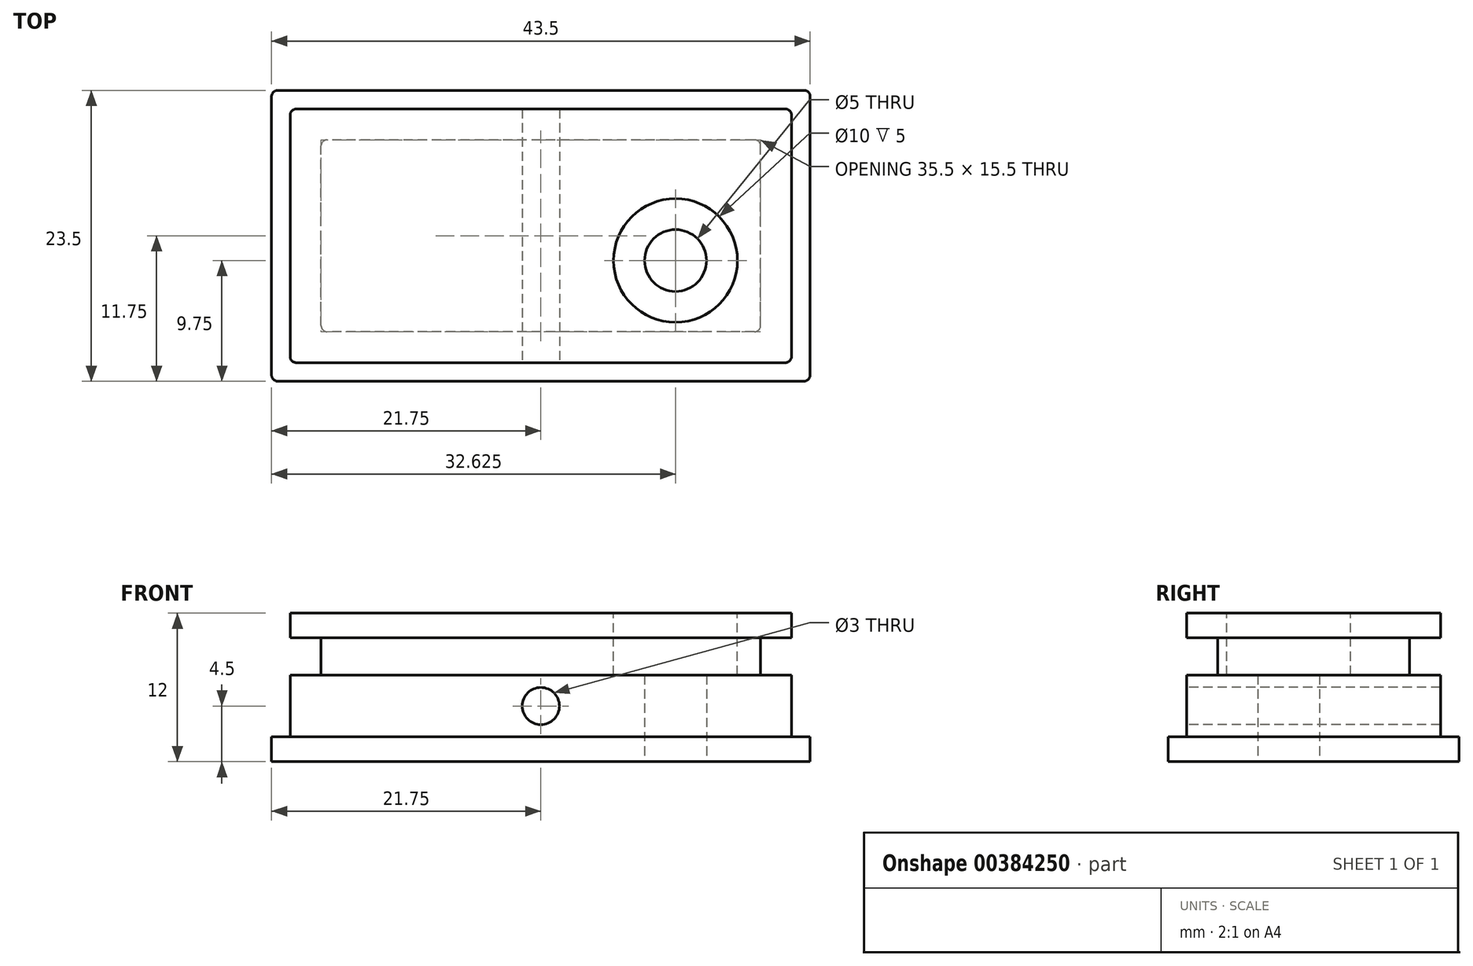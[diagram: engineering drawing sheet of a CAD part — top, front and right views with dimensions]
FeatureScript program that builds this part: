
annotation { "Feature Type Name" : "Feature", "Feature Type Description" : "" }
export const myFeature = defineFeature(function(context is Context, id is Id, definition is map)
    precondition{}
    {
        {
            var Q0;
            Q0=qCreatedBy(makeId("Top.planeOp"),FACE);
            var sketch = newSketch(context, id + "F0", { "sketchPlane" : qUnion([Q0])});
            skLineSegment(sketch, "E0.bottom", {"start": v(21.75, -11.75) * mm, "end": v(-21.75, -11.75) * mm});
            skLineSegment(sketch, "E0.top", {"start": v(21.75, 11.75) * mm, "end": v(-21.75, 11.75) * mm});
            skLineSegment(sketch, "E0.left", {"start": v(21.75, -11.75) * mm, "end": v(21.75, 11.75) * mm});
            skLineSegment(sketch, "E0.right", {"start": v(-21.75, -11.75) * mm, "end": v(-21.75, 11.75) * mm});
            skPoint(sketch, "E0.middle", {"position": v(0, 0) * mm});
            skSolve(sketch);
        }
        {
            var Q0;
            Q0=qSketchRegion(id+"F0",true);
            extrude(context, id + "F1", {"entities" : qUnion([Q0]), "depth" : 2 * mm});
        }
        {
            var Q0;
            Q0=makeQuery(id+"F1.opExtrude","CAP_FACE",FACE,{"disambiguationData":[OSD([sQuery(id+"F0.wireOp",EDGE,"E0.bottom"),sQuery(id+"F0.wireOp",EDGE,"E0.top"),sQuery(id+"F0.wireOp",EDGE,"E0.left"),sQuery(id+"F0.wireOp",EDGE,"E0.right")])],"isStart":false});
            var sketch = newSketch(context, id + "F2", { "sketchPlane" : qUnion([Q0])});
            skLineSegment(sketch, "E1.bottom", {"start": v(21.75, -11.75) * mm, "end": v(-21.75, -11.75) * mm, "construction": true});
            skLineSegment(sketch, "E1.top", {"start": v(21.75, 11.75) * mm, "end": v(-21.75, 11.75) * mm, "construction": true});
            skLineSegment(sketch, "E1.left", {"start": v(21.75, -11.75) * mm, "end": v(21.75, 11.75) * mm, "construction": true});
            skLineSegment(sketch, "E1.right", {"start": v(-21.75, -11.75) * mm, "end": v(-21.75, 11.75) * mm, "construction": true});
            skPoint(sketch, "E1.middle", {"position": v(0, 0) * mm});
            skLineSegment(sketch, "E2.0", {"start": v(20.25, 10.25) * mm, "end": v(-20.25, 10.25) * mm});
            skLineSegment(sketch, "E2.1", {"start": v(20.25, -10.25) * mm, "end": v(20.25, 10.25) * mm});
            skLineSegment(sketch, "E2.2", {"start": v(20.25, -10.25) * mm, "end": v(-20.25, -10.25) * mm});
            skLineSegment(sketch, "E2.3", {"start": v(-20.25, -10.25) * mm, "end": v(-20.25, 10.25) * mm});
            skSolve(sketch);
        }
        {
            var Q0;
            Q0=qSketchRegion(id+"F2",true);
            extrude(context, id + "F3", {"entities" : qUnion([Q0]), "operationType" : NewBodyOperationType.ADD, "depth" : 5 * mm});
        }
        {
            var Q0;
            Q0=makeQuery(id+"F3.opExtrude","CAP_FACE",FACE,{"disambiguationData":[OSD([sQuery(id+"F2.wireOp",EDGE,"E2.0"),sQuery(id+"F2.wireOp",EDGE,"E2.1"),sQuery(id+"F2.wireOp",EDGE,"E2.2"),sQuery(id+"F2.wireOp",EDGE,"E2.3")])],"isStart":false});
            var sketch = newSketch(context, id + "F4", { "sketchPlane" : qUnion([Q0])});
            skLineSegment(sketch, "E3.0", {"start": v(20.25, -10.25) * mm, "end": v(-20.25, -10.25) * mm, "construction": true});
            skLineSegment(sketch, "E4.0", {"start": v(-20.25, -10.25) * mm, "end": v(-20.25, 10.25) * mm, "construction": true});
            skLineSegment(sketch, "E5.0", {"start": v(20.25, 10.25) * mm, "end": v(-20.25, 10.25) * mm, "construction": true});
            skLineSegment(sketch, "E6.0", {"start": v(20.25, -10.25) * mm, "end": v(20.25, 10.25) * mm, "construction": true});
            skLineSegment(sketch, "E7.0", {"start": v(-17.75, -7.75) * mm, "end": v(-17.75, 7.75) * mm});
            skLineSegment(sketch, "E7.1", {"start": v(17.75, -7.75) * mm, "end": v(-17.75, -7.75) * mm});
            skLineSegment(sketch, "E7.2", {"start": v(17.75, -7.75) * mm, "end": v(17.75, 7.75) * mm});
            skLineSegment(sketch, "E7.3", {"start": v(17.75, 7.75) * mm, "end": v(-17.75, 7.75) * mm});
            skSolve(sketch);
        }
        {
            var Q0;
            Q0=qSketchRegion(id+"F4",true);
            var Q1;
            Q1=qConstructionFilter(qBodyType(qCreatedBy(id+"F4",EDGE),BodyType.WIRE),ConstructionObject.NO);
            extrude(context, id + "F5", {"entities" : qUnion([Q0]), "operationType" : NewBodyOperationType.ADD, "surfaceEntities" : qUnion([Q1]), "depth" : 3 * mm});
        }
        {
            var Q0;
            Q0=makeQuery(id+"F5.opExtrude","CAP_FACE",FACE,{"disambiguationData":[OSD([sQuery(id+"F4.wireOp",EDGE,"E7.0"),sQuery(id+"F4.wireOp",EDGE,"E7.1"),sQuery(id+"F4.wireOp",EDGE,"E7.2"),sQuery(id+"F4.wireOp",EDGE,"E7.3")])],"isStart":false});
            var sketch = newSketch(context, id + "F6", { "sketchPlane" : qUnion([Q0])});
            skLineSegment(sketch, "E8.0", {"start": v(20.25, -10.25) * mm, "end": v(-20.25, -10.25) * mm});
            skLineSegment(sketch, "E9.0", {"start": v(20.25, -10.25) * mm, "end": v(20.25, 10.25) * mm});
            skLineSegment(sketch, "E10.0", {"start": v(20.25, 10.25) * mm, "end": v(-20.25, 10.25) * mm});
            skLineSegment(sketch, "E10.1", {"start": v(-20.25, -10.25) * mm, "end": v(-20.25, 10.25) * mm});
            skSolve(sketch);
        }
        {
            var Q0;
            Q0=qSketchRegion(id+"F6",true);
            extrude(context, id + "F7", {"entities" : qUnion([Q0]), "operationType" : NewBodyOperationType.ADD, "depth" : 2 * mm});
        }
        {
            var Q0;
            Q0=makeQuery(id+"F3.opExtrude","SWEPT_EDGE",EDGE,{"disambiguationData":[OSD([sQuery(id+"F2.wireOp",EDGE,"E2.0"),sQuery(id+"F2.wireOp",EDGE,"E2.3")])]});
            var Q1;
            Q1=makeQuery(id+"F5.opExtrude","SWEPT_EDGE",EDGE,{"disambiguationData":[OSD([sQuery(id+"F4.wireOp",EDGE,"E7.0"),sQuery(id+"F4.wireOp",EDGE,"E7.3")])]});
            var Q2;
            Q2=makeQuery(id+"F7.opExtrude","SWEPT_EDGE",EDGE,{"disambiguationData":[OSD([sQuery(id+"F6.wireOp",EDGE,"E10.0"),sQuery(id+"F6.wireOp",EDGE,"E10.1")])]});
            var Q3;
            Q3=makeQuery(id+"F3.opExtrude","SWEPT_EDGE",EDGE,{"disambiguationData":[OSD([sQuery(id+"F2.wireOp",EDGE,"E2.2"),sQuery(id+"F2.wireOp",EDGE,"E2.3")])]});
            var Q4;
            Q4=makeQuery(id+"F5.opExtrude","SWEPT_EDGE",EDGE,{"disambiguationData":[OSD([sQuery(id+"F4.wireOp",EDGE,"E7.0"),sQuery(id+"F4.wireOp",EDGE,"E7.1")])]});
            var Q5;
            Q5=makeQuery(id+"F7.opExtrude","SWEPT_EDGE",EDGE,{"disambiguationData":[OSD([sQuery(id+"F6.wireOp",EDGE,"E8.0"),sQuery(id+"F6.wireOp",EDGE,"E10.1")])]});
            var Q6;
            Q6=makeQuery(id+"F3.opExtrude","SWEPT_EDGE",EDGE,{"disambiguationData":[OSD([sQuery(id+"F2.wireOp",EDGE,"E2.1"),sQuery(id+"F2.wireOp",EDGE,"E2.2")])]});
            var Q7;
            Q7=makeQuery(id+"F5.opExtrude","SWEPT_EDGE",EDGE,{"disambiguationData":[OSD([sQuery(id+"F4.wireOp",EDGE,"E7.1"),sQuery(id+"F4.wireOp",EDGE,"E7.2")])]});
            var Q8;
            Q8=makeQuery(id+"F7.opExtrude","SWEPT_EDGE",EDGE,{"disambiguationData":[OSD([sQuery(id+"F6.wireOp",EDGE,"E8.0"),sQuery(id+"F6.wireOp",EDGE,"E9.0")])]});
            var Q9;
            Q9=makeQuery(id+"F3.opExtrude","SWEPT_EDGE",EDGE,{"disambiguationData":[OSD([sQuery(id+"F2.wireOp",EDGE,"E2.0"),sQuery(id+"F2.wireOp",EDGE,"E2.1")])]});
            var Q10;
            Q10=makeQuery(id+"F5.opExtrude","SWEPT_EDGE",EDGE,{"disambiguationData":[OSD([sQuery(id+"F4.wireOp",EDGE,"E7.2"),sQuery(id+"F4.wireOp",EDGE,"E7.3")])]});
            var Q11;
            Q11=makeQuery(id+"F7.opExtrude","SWEPT_EDGE",EDGE,{"disambiguationData":[OSD([sQuery(id+"F6.wireOp",EDGE,"E9.0"),sQuery(id+"F6.wireOp",EDGE,"E10.0")])]});
            var Q12;
            Q12=makeQuery(id+"F1.opExtrude","SWEPT_EDGE",EDGE,{"disambiguationData":[OSD([sQuery(id+"F0.wireOp",EDGE,"E0.bottom"),sQuery(id+"F0.wireOp",EDGE,"E0.left")])]});
            var Q13;
            Q13=makeQuery(id+"F1.opExtrude","SWEPT_EDGE",EDGE,{"disambiguationData":[OSD([sQuery(id+"F0.wireOp",EDGE,"E0.top"),sQuery(id+"F0.wireOp",EDGE,"E0.left")])]});
            var Q14;
            Q14=makeQuery(id+"F1.opExtrude","SWEPT_EDGE",EDGE,{"disambiguationData":[OSD([sQuery(id+"F0.wireOp",EDGE,"E0.bottom"),sQuery(id+"F0.wireOp",EDGE,"E0.right")])]});
            var Q15;
            Q15=makeQuery(id+"F1.opExtrude","SWEPT_EDGE",EDGE,{"disambiguationData":[OSD([sQuery(id+"F0.wireOp",EDGE,"E0.top"),sQuery(id+"F0.wireOp",EDGE,"E0.right")])]});
            fillet(context, id + "F8", {"entities" : qUnion([Q0, Q1, Q2, Q3, Q4, Q5, Q6, Q7, Q8, Q9, Q10, Q11, Q12, Q13, Q14, Q15]), "radius" : 0.5 * mm, "tangentPropagation" : true, "allowEdgeOverflow" : false});
        }
        {
            var Q0;
            Q0=qCreatedBy(makeId("Top.planeOp"),FACE);
            var sketch = newSketch(context, id + "F9", { "sketchPlane" : qUnion([Q0])});
            skCircle(sketch, "E11", {"center": v(10.88, -2) * mm, "radius": 2.5 * mm});
            skLineSegment(sketch, "E12", {"start": v(0, -11.75) * mm, "end": v(0, 0) * mm, "construction": true});
            skLineSegment(sketch, "E13", {"start": v(0, 0) * mm, "end": v(21.75, 0) * mm, "construction": true});
            skLineSegment(sketch, "E14", {"start": v(0, -2) * mm, "end": v(21.75, -2) * mm, "construction": true});
            skLineSegment(sketch, "E15", {"start": v(10.88, 0) * mm, "end": v(10.88, -11.75) * mm, "construction": true});
            skSolve(sketch);
        }
        {
            var Q0;
            Q0=qSketchRegion(id+"F9",true);
            var Q1;
            Q1=makeQuery(id+"F7.opExtrude","CAP_FACE",FACE,{"disambiguationData":[OSD([sQuery(id+"F6.wireOp",EDGE,"E8.0"),sQuery(id+"F6.wireOp",EDGE,"E9.0"),sQuery(id+"F6.wireOp",EDGE,"E10.0"),sQuery(id+"F6.wireOp",EDGE,"E10.1")])],"isStart":false});
            extrude(context, id + "F10", {"entities" : qUnion([Q0]), "operationType" : NewBodyOperationType.REMOVE, "endBound" : BoundingType.THROUGH_ALL, "endBoundEntityFace" : qUnion([Q1]), "depth" : 25 * mm});
        }
        {
            var Q0;
            Q0=makeQuery(id+"F7.opExtrude","CAP_FACE",FACE,{"disambiguationData":[OSD([sQuery(id+"F6.wireOp",EDGE,"E8.0"),sQuery(id+"F6.wireOp",EDGE,"E9.0"),sQuery(id+"F6.wireOp",EDGE,"E10.0"),sQuery(id+"F6.wireOp",EDGE,"E10.1")])],"isStart":false});
            var sketch = newSketch(context, id + "F11", { "sketchPlane" : qUnion([Q0])});
            skCircle(sketch, "E16", {"center": v(10.88, -2) * mm, "radius": 5 * mm});
            skSolve(sketch);
        }
        {
            var Q0;
            Q0=qSketchRegion(id+"F11",true);
            var Q1;
            Q1=makeQuery(id+"F3.opExtrude","CAP_FACE",FACE,{"disambiguationData":[OSD([sQuery(id+"F2.wireOp",EDGE,"E2.0"),sQuery(id+"F2.wireOp",EDGE,"E2.1"),sQuery(id+"F2.wireOp",EDGE,"E2.2"),sQuery(id+"F2.wireOp",EDGE,"E2.3")])],"isStart":false});
            extrude(context, id + "F12", {"entities" : qUnion([Q0]), "operationType" : NewBodyOperationType.REMOVE, "endBound" : BoundingType.UP_TO_SURFACE, "oppositeDirection" : true, "endBoundEntityFace" : qUnion([Q1]), "depth" : 5.8 * mm});
        }
        {
            var Q0;
            Q0=makeQuery(id+"F3.opExtrude","SWEPT_FACE",FACE,{"disambiguationData":[OSD([sQuery(id+"F2.wireOp",EDGE,"E2.2")])]});
            var sketch = newSketch(context, id + "F13", { "sketchPlane" : qUnion([Q0])});
            skLineSegment(sketch, "E17", {"start": v(0, 2) * mm, "end": v(0, 7) * mm, "construction": true});
            skCircle(sketch, "E18", {"center": v(0, 4.5) * mm, "radius": 1.5 * mm});
            skSolve(sketch);
        }
        {
            var Q0;
            Q0=qSketchRegion(id+"F13",true);
            extrude(context, id + "F14", {"entities" : qUnion([Q0]), "operationType" : NewBodyOperationType.REMOVE, "oppositeDirection" : true, "depth" : 25 * mm});
        }
    });
